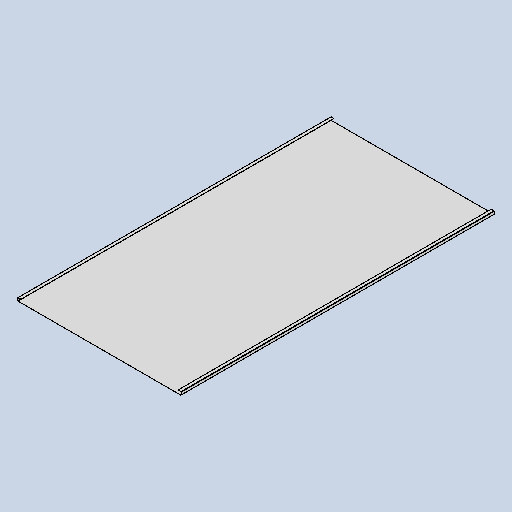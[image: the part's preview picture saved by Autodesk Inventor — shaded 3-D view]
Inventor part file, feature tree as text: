
AUTODESK INVENTOR PART (.ipt)
format: ipt  version: 2025 (Build 290162010, 162A)  size: 200,704 bytes
history: native  units: mm
features: sheet_metal_op x13, other x6, sketch x5, chamfer x1
ambient origin geometry x8: Origin, YZ Plane, XZ Plane, XY Plane, X Axis, Y Axis, Z Axis, Center Point
bodies: Body1 (feature_tree)
feature tree (25):
  sheet_metal_op  "Face1"
  sheet_metal_op  "Flange2"
  sheet_metal_op  "Flange3"
  sheet_metal_op  "Flange4"
  sheet_metal_op  "Flange5"
  chamfer  "Corner Round1"
  sketch  "Sketch6"  dims[d12=23.212879mm]
  other  "Plate2"
  sketch  "Sketch11"  dims[d52=511.8mm]
  other  "Plate4"
  sheet_metal_op  "Bend3"
  sheet_metal_op  "Corner3"
  sketch  "Sketch12"  dims[d53=980.0mm]
  other  "Plate5"
  sheet_metal_op  "Bend4"
  sheet_metal_op  "Corner4"
  sketch  "Sketch13"  dims[d54=0.5mm]
  other  "Plate6"
  sheet_metal_op  "Bend5"
  sheet_metal_op  "Corner5"
  sketch  "Sketch14"  dims[d84=0.5mm d85=0.25mm d86=1.0mm d87=0.5mm d88=10.0mm d89=90.0deg d90=0.5mm d91=2.0mm d92=0.5mm d93=0.5mm d94=0.5mm d95=0.25mm d96=1.0mm d97=0.5mm d98=10.0mm d99=90.0deg d100=0.5mm d101=2.0mm d102=0.5mm d103=0.5mm d104=0.5mm d105=0.25mm d106=1.0mm d107=0.5mm d108=10.0mm d109=90.0deg d110=0.5mm d111=2.0mm d112=0.5mm d113=0.5mm d114=0.5mm d115=0.25mm d116=1.0mm d117=0.5mm d118=10.0mm d119=90.0deg d120=0.5mm d121=2.0mm d122=0.5mm d123=0.5mm d124=4.0mm]
  other  "Plate7"
  sheet_metal_op  "Bend6"
  sheet_metal_op  "Corner6"
  other  "Definition1"
